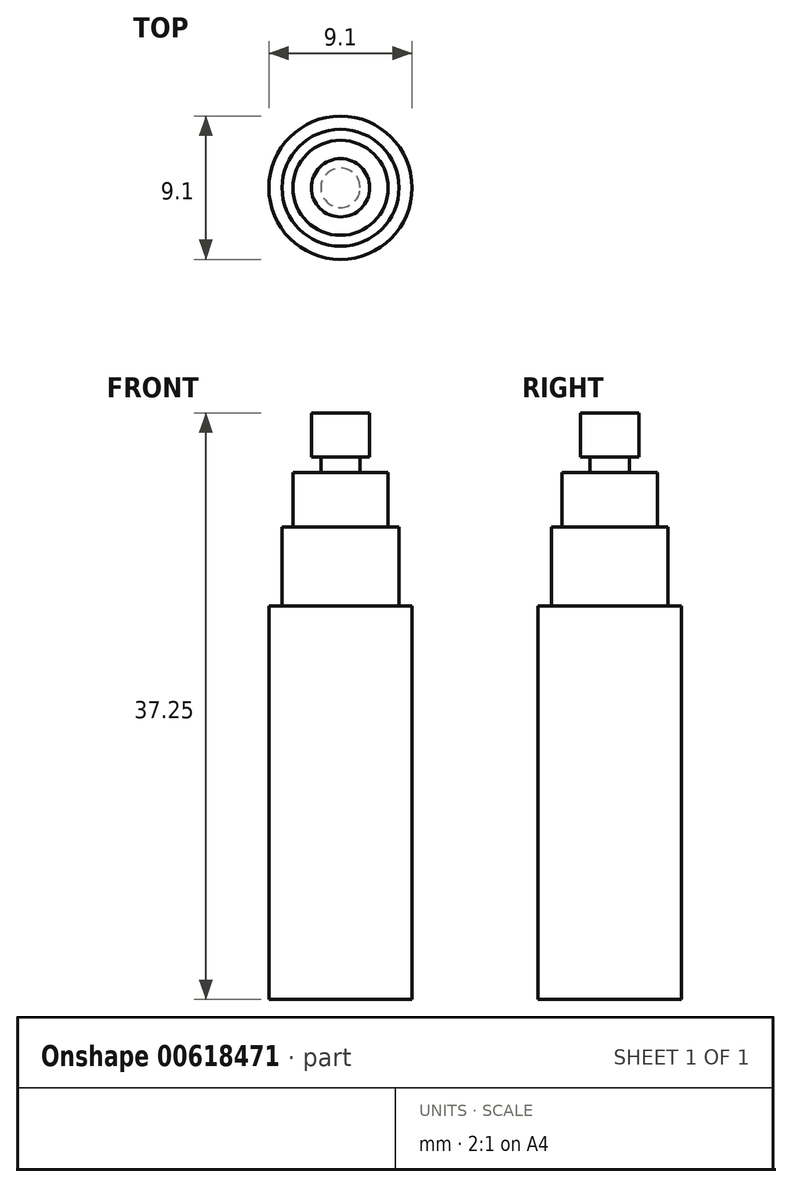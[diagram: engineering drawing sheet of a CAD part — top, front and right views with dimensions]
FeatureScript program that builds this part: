
annotation { "Feature Type Name" : "Feature", "Feature Type Description" : "" }
export const myFeature = defineFeature(function(context is Context, id is Id, definition is map)
    precondition{}
    {
        {
            var Q0;
            Q0=qCreatedBy(makeId("Top.planeOp"),FACE);
            var sketch = newSketch(context, id + "F0", { "sketchPlane" : qUnion([Q0])});
            skCircle(sketch, "E0", {"center": v(0, 0) * mm, "radius": 4.55 * mm});
            skSolve(sketch);
        }
        {
            var Q0;
            Q0=qSketchRegion(id+"F0",true);
            extrude(context, id + "F1", {"entities" : qUnion([Q0]), "depth" : 25 * mm, "offsetDistance" : 25 * mm});
        }
        {
            var Q0;
            Q0=makeQuery(id+"F1.opExtrude","CAP_FACE",FACE,{"disambiguationData":[OSD([sQuery(id+"F0.wireOp",EDGE,"E0")])],"isStart":false});
            var sketch = newSketch(context, id + "F2", { "sketchPlane" : qUnion([Q0])});
            skCircle(sketch, "E1", {"center": v(0, 0) * mm, "radius": 3.71 * mm});
            skSolve(sketch);
        }
        {
            var Q0;
            Q0=makeQuery(id+"F2.imprint","IMPRINT",FACE,{"disambiguationData":[TD([[makeQuery(id+"F2.imprint","IMPRINT",EDGE,{"derivedFrom":sQuery(id+"F2.wireOp",EDGE,"E1")}),1.0]])]});
            extrude(context, id + "F3", {"entities" : qUnion([Q0]), "operationType" : NewBodyOperationType.ADD, "depth" : 5 * mm, "offsetDistance" : 25 * mm});
        }
        {
            var Q0;
            Q0=makeQuery(id+"F3.opExtrude","CAP_FACE",FACE,{"disambiguationData":[OSD([sQuery(id+"F2.wireOp",EDGE,"E1")])],"isStart":false});
            var sketch = newSketch(context, id + "F4", { "sketchPlane" : qUnion([Q0])});
            skCircle(sketch, "E2", {"center": v(0, 0) * mm, "radius": 3.02 * mm});
            skSolve(sketch);
        }
        {
            var Q0;
            Q0=makeQuery(id+"F4.imprint","IMPRINT",FACE,{"disambiguationData":[TD([[makeQuery(id+"F4.imprint","IMPRINT",EDGE,{"derivedFrom":sQuery(id+"F4.wireOp",EDGE,"E2")}),1.0]])]});
            extrude(context, id + "F5", {"entities" : qUnion([Q0]), "operationType" : NewBodyOperationType.ADD, "depth" : 3.45 * mm, "offsetDistance" : 25 * mm});
        }
        {
            var Q0;
            Q0=makeQuery(id+"F5.opExtrude","CAP_FACE",FACE,{"disambiguationData":[OSD([sQuery(id+"F4.wireOp",EDGE,"E2")])],"isStart":false});
            var sketch = newSketch(context, id + "F6", { "sketchPlane" : qUnion([Q0])});
            skCircle(sketch, "E3", {"center": v(0, 0) * mm, "radius": 1.25 * mm});
            skSolve(sketch);
        }
        {
            var Q0;
            Q0=makeQuery(id+"F6.imprint","IMPRINT",FACE,{"disambiguationData":[TD([[makeQuery(id+"F6.imprint","IMPRINT",EDGE,{"derivedFrom":sQuery(id+"F6.wireOp",EDGE,"E3")}),1.0]])]});
            extrude(context, id + "F7", {"entities" : qUnion([Q0]), "operationType" : NewBodyOperationType.ADD, "depth" : 1 * mm, "offsetDistance" : 25 * mm});
        }
        {
            var Q0;
            Q0=makeQuery(id+"F7.opExtrude","CAP_FACE",FACE,{"disambiguationData":[OSD([sQuery(id+"F6.wireOp",EDGE,"E3")])],"isStart":false});
            var sketch = newSketch(context, id + "F8", { "sketchPlane" : qUnion([Q0])});
            skCircle(sketch, "E4", {"center": v(0, 0) * mm, "radius": 1.85 * mm});
            skSolve(sketch);
        }
        {
            var Q0;
            Q0=makeQuery(id+"F8.imprint","IMPRINT",FACE,{"disambiguationData":[TD([[makeQuery(id+"F8.imprint","IMPRINT",EDGE,{"derivedFrom":makeQuery(id+"F7.opExtrude","CAP_EDGE",EDGE,{"disambiguationData":[OSD([sQuery(id+"F6.wireOp",EDGE,"E3")])],"isStart":false})}),1.0]])]});
            var Q1;
            Q1=makeQuery(id+"F8.imprint","IMPRINT",FACE,{"disambiguationData":[TD([[makeQuery(id+"F8.imprint","IMPRINT",EDGE,{"derivedFrom":sQuery(id+"F8.wireOp",EDGE,"E4")}),1.0]])]});
            extrude(context, id + "F9", {"entities" : qUnion([Q0, Q1]), "operationType" : NewBodyOperationType.ADD, "depth" : 2.8 * mm, "offsetDistance" : 25 * mm});
        }
    });
